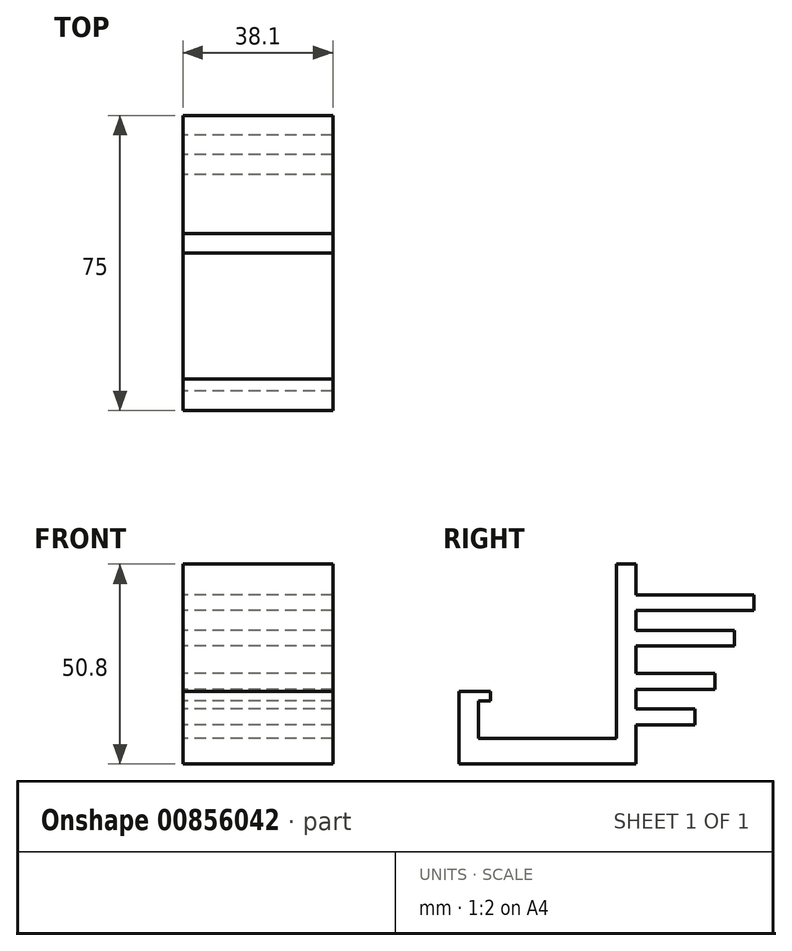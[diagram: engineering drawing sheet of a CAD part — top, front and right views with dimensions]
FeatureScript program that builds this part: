
annotation { "Feature Type Name" : "Feature", "Feature Type Description" : "" }
export const myFeature = defineFeature(function(context is Context, id is Id, definition is map)
    precondition{}
    {
        {
            var Q0;
            Q0=qCreatedBy(makeId("Right.planeOp"),FACE);
            var sketch = newSketch(context, id + "F0", { "sketchPlane" : qUnion([Q0])});
            skLineSegment(sketch, "E0.bottom", {"start": v(0, 0) * mm, "end": v(5, 0) * mm});
            skLineSegment(sketch, "E0.top", {"start": v(0, 50.8) * mm, "end": v(5, 50.8) * mm});
            skLineSegment(sketch, "E0.left", {"start": v(0, 0) * mm, "end": v(0, 50.8) * mm});
            skLineSegment(sketch, "E0.right", {"start": v(5, 0) * mm, "end": v(5, 50.8) * mm});
            skLineSegment(sketch, "E1.bottom", {"start": v(0, 0) * mm, "end": v(-40, 0) * mm});
            skLineSegment(sketch, "E1.top", {"start": v(0, 6.5) * mm, "end": v(-40, 6.5) * mm});
            skLineSegment(sketch, "E1.left", {"start": v(0, 0) * mm, "end": v(0, 6.5) * mm});
            skLineSegment(sketch, "E1.right", {"start": v(-40, 0) * mm, "end": v(-40, 6.5) * mm});
            skLineSegment(sketch, "E2.bottom", {"start": v(-40, 6.5) * mm, "end": v(-35, 6.5) * mm});
            skLineSegment(sketch, "E2.top", {"start": v(-40, 16) * mm, "end": v(-35, 16) * mm});
            skLineSegment(sketch, "E2.left", {"start": v(-40, 6.5) * mm, "end": v(-40, 16) * mm});
            skLineSegment(sketch, "E2.right", {"start": v(-35, 6.5) * mm, "end": v(-35, 16) * mm});
            skLineSegment(sketch, "E3.bottom", {"start": v(5, 23) * mm, "end": v(25, 23) * mm});
            skLineSegment(sketch, "E3.top", {"start": v(5, 19) * mm, "end": v(25, 19) * mm});
            skLineSegment(sketch, "E3.left", {"start": v(5, 23) * mm, "end": v(5, 19) * mm});
            skLineSegment(sketch, "E3.right", {"start": v(25, 23) * mm, "end": v(25, 19) * mm});
            skLineSegment(sketch, "E4.bottom", {"start": v(5, 14) * mm, "end": v(20, 14) * mm});
            skLineSegment(sketch, "E4.top", {"start": v(5, 10) * mm, "end": v(20, 10) * mm});
            skLineSegment(sketch, "E4.left", {"start": v(5, 14) * mm, "end": v(5, 10) * mm});
            skLineSegment(sketch, "E4.right", {"start": v(20, 14) * mm, "end": v(20, 10) * mm});
            skLineSegment(sketch, "E5.bottom", {"start": v(5, 43) * mm, "end": v(35, 43) * mm});
            skLineSegment(sketch, "E5.top", {"start": v(5, 39) * mm, "end": v(35, 39) * mm});
            skLineSegment(sketch, "E5.left", {"start": v(5, 43) * mm, "end": v(5, 39) * mm});
            skLineSegment(sketch, "E5.right", {"start": v(35, 43) * mm, "end": v(35, 39) * mm});
            skLineSegment(sketch, "E6.bottom", {"start": v(5, 34) * mm, "end": v(30, 34) * mm});
            skLineSegment(sketch, "E6.top", {"start": v(5, 30) * mm, "end": v(30, 30) * mm});
            skLineSegment(sketch, "E6.left", {"start": v(5, 34) * mm, "end": v(5, 30) * mm});
            skLineSegment(sketch, "E6.right", {"start": v(30, 34) * mm, "end": v(30, 30) * mm});
            skLineSegment(sketch, "E7.bottom", {"start": v(-40, 16) * mm, "end": v(-32, 16) * mm});
            skLineSegment(sketch, "E7.top", {"start": v(-40, 18.5) * mm, "end": v(-32, 18.5) * mm});
            skLineSegment(sketch, "E7.left", {"start": v(-40, 16) * mm, "end": v(-40, 18.5) * mm});
            skLineSegment(sketch, "E7.right", {"start": v(-32, 16) * mm, "end": v(-32, 18.5) * mm});
            skSolve(sketch);
        }
        {
            var Q0;
            Q0 = qSketchRegion(id + "F0", true);
            extrude(context, id + "F1", {"entities" : qUnion([Q0]), "depth" : 38.1 * mm, "offsetDistance" : 25.4 * mm});
        }
    });
